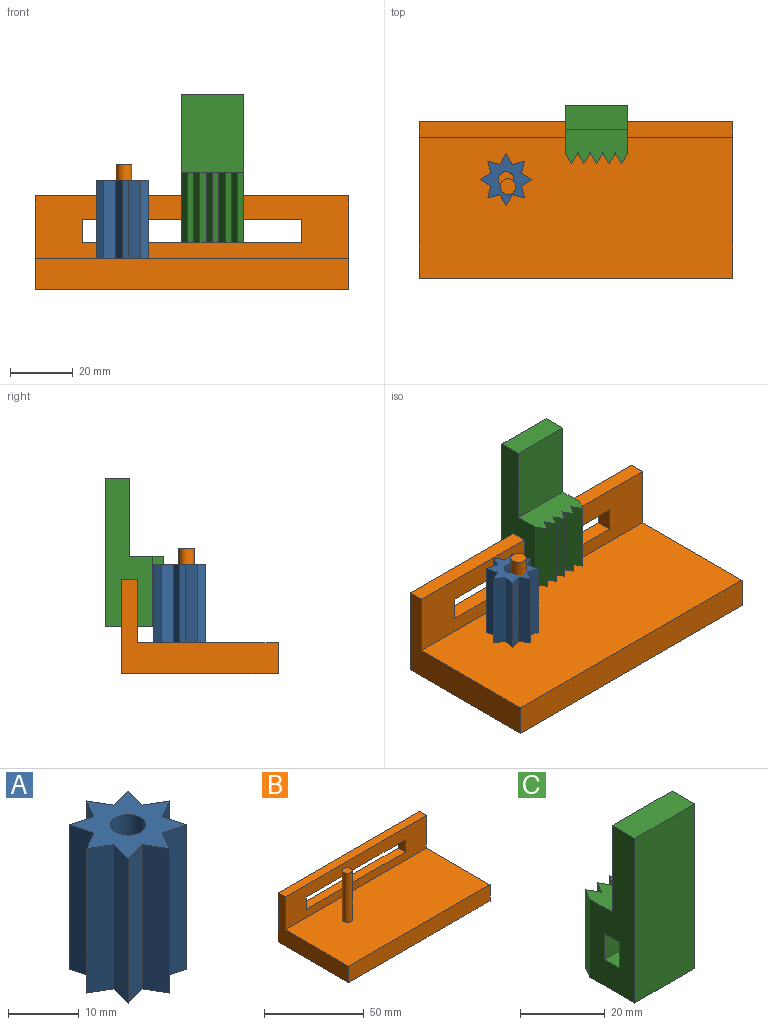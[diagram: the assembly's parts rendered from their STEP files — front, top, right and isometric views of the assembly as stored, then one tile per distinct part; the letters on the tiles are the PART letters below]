
ASSEMBLY  parts=3 mates=3
PART A: 19 faces, bbox 16.6x16.6x25 mm
  f0: plane 25x3.46mm, normal (-0.87,0.5,0), area 100mm2, adj f1,f15,f17,f18
  f1: plane 25x3.86mm, normal (0.26,0.97,0), area 100mm2, adj f0,f2,f17,f18
  f2: plane 25x3.86mm, normal (-0.97,-0.26,0), area 100mm2, adj f1,f3,f17,f18
  f3: plane 25x3.46mm, normal (-0.5,0.87,0), area 100mm2, adj f2,f4,f17,f18
  f4: plane 25x3.46mm, normal (-0.5,-0.87,0), area 100mm2, adj f3,f5,f17,f18
  f5: plane 25x3.86mm, normal (-0.97,0.26,0), area 100mm2, adj f4,f6,f17,f18
  f6: plane 25x3.86mm, normal (0.26,-0.97,0), area 100mm2, adj f5,f7,f17,f18
  f7: plane 25x3.46mm, normal (-0.87,-0.5,0), area 100mm2, adj f6,f8,f17,f18
  f8: plane 25x3.46mm, normal (0.87,-0.5,0), area 100mm2, adj f7,f9,f17,f18
  f9: plane 25x3.86mm, normal (-0.26,-0.97,0), area 100mm2, adj f8,f10,f17,f18
  f10: plane 25x3.86mm, normal (0.97,0.26,0), area 100mm2, adj f9,f11,f17,f18
  f11: plane 25x3.46mm, normal (0.5,-0.87,0), area 100mm2, adj f10,f12,f17,f18
  f12: plane 25x3.46mm, normal (0.5,0.87,0), area 100mm2, adj f11,f13,f17,f18
  f13: plane 25x3.86mm, normal (0.97,-0.26,0), area 100mm2, adj f12,f14,f17,f18
  f14: plane 25x3.86mm, normal (-0.26,0.97,0), area 100mm2, adj f13,f15,f17,f18
  f15: plane 25x3.46mm, normal (0.87,0.5,0), area 100mm2, adj f0,f14,f17,f18
  f16: cylinder r=2.5mm len=25mm, axis (0,0,-1), area 392.7mm2, adj f17,f18
  f17: plane 16.59x16.59mm, normal (0,0,1), area 113mm2, adj f0,f1,f2,f3,f4,f5,f6,f7
  f18: plane 16.59x16.59mm, normal (0,0,-1), area 113mm2, adj f0,f1,f2,f3,f4,f5,f6,f7
PART B: 14 faces, bbox 100x50x40 mm
  f0: plane 50x30mm, normal (-1,0,0), area 600mm2, adj f1,f3,f4,f5,f9,f11
  f1: plane 100x10mm, normal (0,-1,0), area 1000mm2, adj f0,f2,f4,f5
  f2: plane 50x30mm, normal (1,0,0), area 600mm2, adj f1,f3,f4,f5,f9,f11
  f3: plane 100x30mm, normal (0,1,0), area 2475mm2, adj f0,f2,f5,f6,f7,f8,f9,f10
  f4: plane 100x45mm, normal (0,0,1), area 4480.4mm2, adj f0,f1,f2,f11,f12
  f5: plane 100x50mm, normal (0,0,-1), area 5000mm2, adj f0,f1,f2,f3
  f6: plane 7.5x5mm, normal (-1,0,0), area 37.5mm2, adj f3,f7,f10,f11
  f7: plane 70x5mm, normal (0,0,-1), area 350mm2, adj f3,f6,f8,f11
  f8: plane 7.5x5mm, normal (1,0,0), area 37.5mm2, adj f3,f7,f10,f11
  f9: plane 100x5mm, normal (0,0,1), area 500mm2, adj f0,f2,f3,f11
  f10: plane 70x5mm, normal (0,0,1), area 350mm2, adj f3,f6,f8,f11
  f11: plane 100x20mm, normal (0,-1,0), area 1475mm2, adj f0,f2,f4,f6,f7,f8,f9,f10
  f12: cylinder r=2.5mm len=30mm, axis (0,0,-1), area 471.2mm2, adj f4,f13
  f13: plane 5x5mm, normal (0,0,1), area 19.6mm2, adj f12
PART C: 21 faces, bbox 20x18.5x47.5 mm
  f0: plane 20x5mm, normal (0,0,1), area 100mm2, adj f1,f3,f5,f6
  f1: plane 47.5x15mm, normal (-1,0,0), area 487.5mm2, adj f0,f2,f4,f5,f6,f7,f8,f17
  f2: plane 20x18.46mm, normal (0,0,-1), area 334.6mm2, adj f1,f3,f4,f9,f10,f11,f12,f13
  f3: plane 47.5x15mm, normal (1,0,0), area 487.5mm2, adj f0,f2,f4,f5,f6,f7,f8,f9
  f4: plane 47.5x20mm, normal (0,-1,0), area 950mm2, adj f1,f2,f3,f20
  f5: plane 20x7.5mm, normal (0,1,0), area 150mm2, adj f0,f1,f3,f7
  f6: plane 20x7.5mm, normal (0,-1,0), area 150mm2, adj f0,f1,f3,f7
  f7: plane 20x5mm, normal (0,0,-1), area 100mm2, adj f1,f3,f5,f6
  f8: plane 20x10.96mm, normal (0,0,1), area 184.6mm2, adj f1,f3,f9,f10,f11,f12,f13,f14
  f9: plane 22.5x3.46mm, normal (0.87,0.5,0), area 90mm2, adj f2,f3,f8,f10
  f10: plane 22.5x3.46mm, normal (-0.87,0.5,0), area 90mm2, adj f2,f8,f9,f11
  f11: plane 22.5x3.46mm, normal (0.87,0.5,0), area 90mm2, adj f2,f8,f10,f12
  f12: plane 22.5x3.46mm, normal (-0.87,0.5,0), area 90mm2, adj f2,f8,f11,f13
  f13: plane 22.5x3.46mm, normal (0.87,0.5,0), area 90mm2, adj f2,f8,f12,f14
  f14: plane 22.5x3.46mm, normal (-0.87,0.5,0), area 90mm2, adj f2,f8,f13,f15
  f15: plane 22.5x3.46mm, normal (0.87,0.5,0), area 90mm2, adj f2,f8,f14,f16
  f16: plane 22.5x3.46mm, normal (-0.87,0.5,0), area 90mm2, adj f2,f8,f15,f18
  f17: plane 22.5x3.46mm, normal (-0.87,0.5,0), area 90mm2, adj f1,f2,f8,f18
  f18: plane 22.5x3.46mm, normal (0.87,0.5,0), area 90mm2, adj f2,f8,f16,f17
  f19: plane 25x20mm, normal (0,1,0), area 500mm2, adj f1,f3,f8,f20
  f20: plane 20x7.5mm, normal (0,0,1), area 150mm2, adj f1,f3,f4,f19
PLACE A t=(-3.95,16.92,70.48)mm
PLACE B t=(16.38,5.6,60.48)mm
PLACE C rot(axis=(0,0,1),180deg) t=(12.94,20.6,75.48)mm
MATE planar C.f0 <-> B.f7  axis (0,0,1) through (32.94,28.1,82.98)mm
MATE planar A.f18 <-> B.f4  axis (0,0,1) through (-11.81,6.23,70.48)mm
MATE planar C.f6 <-> B.f11  axis (0,1,0) through (12.94,25.6,86.73)mm
